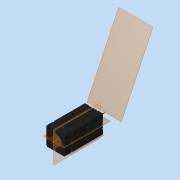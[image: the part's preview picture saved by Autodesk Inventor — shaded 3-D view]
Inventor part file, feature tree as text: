
AUTODESK INVENTOR PART (.ipt)
format: ipt  version: 2019.4 (Build 234330000, 330)  size: 325,120 bytes
history: native  units: in
note: dims shown in document units (in); Inventor stores cm internally (conversion verified against a paired STEP export)
features: sketch x8, extrude x7, projected_geometry x6, plane x4, other x3, pattern_circular x2, reference x2, hole x1
ambient origin geometry x8: Origin, YZ Plane, XZ Plane, XY Plane, X Axis, Y Axis, Z Axis, Center Point
bodies: Solid1 (feature_tree)
feature tree (33):
  extrude  "Extrusion1"  Depth=1.1772in
  extrude  "Extrusion2"  Depth=1.8988in TaperAngle=0.0deg
  extrude  "Extrusion3"  Depth=0.2756in TaperAngle=0.0deg
  pattern_circular  "Circular Pattern1"  [2 undecoded]
  hole  "Hole1"  [1 undecoded]
  extrude  "Extrusion4"  Depth=0.0787in
  extrude  "Extrusion5"  Depth=0.0394in TaperAngle=0.0deg
  plane  "Work Plane1"
  other  "Work Axis1"
  plane  "Work Plane2"
  plane  "Work Plane3"
  extrude  "Extrusion7"  Depth=0.3937in TaperAngle=360.0deg
  pattern_circular  "Circular Pattern2"  [2 undecoded]
  plane  "Work Plane4"
  extrude  "Extrusion8"  Depth=0.3937in
  sketch  "Sketch1"  dims[d0=1.1772in d1=1.1772in]
  sketch  "Sketch2"  dims[d2=0.0787in d3=1.8988in d4=0.0in]
  projected_geometry  "Projected Loop1"
  sketch  "Sketch3"  dims[d5=0.5in d6=0.2756in d7=0.0in]
  projected_geometry  "Projected Loop2"
  sketch  "Sketch4"  dims[d8=0.0787in]
  projected_geometry  "Projected Loop3"
  projected_geometry  "Projected Loop4"
  sketch  "Sketch5"  dims[d9=0.0394in]
  sketch  "Sketch6"  dims[d10=0.0787in]
  projected_geometry  "Projected Loop5"
  sketch  "Sketch8"  dims[d11=0.0787in]
  projected_geometry  "Projected Loop6"
  sketch  "Sketch9"  dims[d12=0.0787in d13=0.0394in d14=0.0787in d15=0.0787in d16=0.0394in d17=0.0in d18=1.5748in d19=360.0deg d21=0.9646in d22=0.9646in d23=0.2677in d24=0.2677in d25=0.1102in d26=0.2362in d27=0.2362in d28=0.0984in d29=90.0deg d30=0.4724in d31=0.8108in d32=0.8661in d33=0.8661in d34=0.0787in d35=0.0787in d36=0.0787in d37=0.0787in d38=0.1181in d39=0.0in d40=0.0787in d41=0.3701in d42=0.0in d43=0.0984in d46=0.0394in d47=0.3937in d48=0.0in d49=1.5748in d50=360.0deg d52=0.3937in d53=0.0in]
  reference  "Reference1"
  reference  "Reference2"
  other  "Assembly_openSIM_module_v2.iam"
  other  "30_CUBE_openSIM_base_v2:1"
note: 5 required parameter values undecoded (feature->parameter linkage not recoverable at this tier; creation-order binding heuristic only, values carry confidence <= 0.55)
